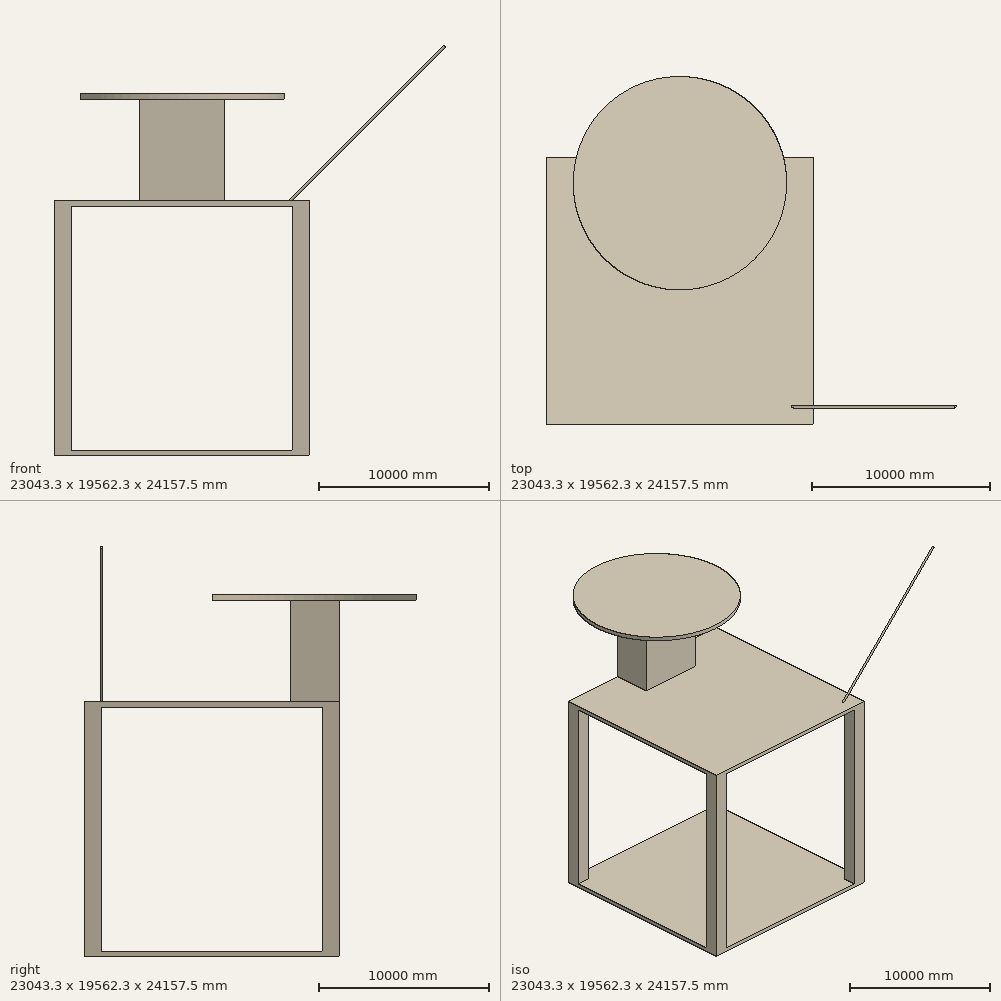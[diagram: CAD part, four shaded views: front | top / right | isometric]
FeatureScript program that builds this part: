
annotation { "Feature Type Name" : "Feature", "Feature Type Description" : "" }
export const myFeature = defineFeature(function(context is Context, id is Id, definition is map)
    precondition{}
    {
        {
            var Q0;
            Q0=qCreatedBy(makeId("Top.planeOp"),FACE);
            var sketch = newSketch(context, id + "F0", { "sketchPlane" : qUnion([Q0])});
            skLineSegment(sketch, "E0.bottom", {"start": v(-7500, 7500) * mm, "end": v(7500, 7500) * mm});
            skLineSegment(sketch, "E0.top", {"start": v(-7500, -7500) * mm, "end": v(7500, -7500) * mm});
            skLineSegment(sketch, "E0.left", {"start": v(-7500, 7500) * mm, "end": v(-7500, -7500) * mm});
            skLineSegment(sketch, "E0.right", {"start": v(7500, 7500) * mm, "end": v(7500, -7500) * mm});
            skSolve(sketch);
        }
        {
            var Q0;
            Q0=makeQuery(id+"F0.imprint","IMPRINT",FACE,{"disambiguationData":[TD([[makeQuery(id+"F0.imprint","IMPRINT",EDGE,{"derivedFrom":sQuery(id+"F0.wireOp",EDGE,"E0.bottom")}),-1.0]])]});
            extrude(context, id + "F1", {"entities" : qUnion([Q0]), "depth" : 15000 * mm, "offsetDistance" : 25 * mm});
        }
        {
            var Q0;
            Q0=makeQuery(id+"F1.opExtrude","SWEPT_FACE",FACE,{"disambiguationData":[OSD([sQuery(id+"F0.wireOp",EDGE,"E0.top")])]});
            var sketch = newSketch(context, id + "F2", { "sketchPlane" : qUnion([Q0])});
            skLineSegment(sketch, "E1", {"start": v(-6500, 300) * mm, "end": v(6500, 300) * mm});
            skLineSegment(sketch, "E2", {"start": v(-6500, 300) * mm, "end": v(-6500, 14700) * mm});
            skLineSegment(sketch, "E3", {"start": v(-6500, 14700) * mm, "end": v(6500, 14700) * mm});
            skLineSegment(sketch, "E4", {"start": v(6500, 14700) * mm, "end": v(6500, 300) * mm});
            skSolve(sketch);
        }
        {
            var Q0;
            Q0=makeQuery(id+"F2.imprint","IMPRINT",FACE,{"disambiguationData":[TD([[makeQuery(id+"F2.imprint","IMPRINT",EDGE,{"derivedFrom":sQuery(id+"F2.wireOp",EDGE,"E1")}),1.0]])]});
            extrude(context, id + "F3", {"entities" : qUnion([Q0]), "operationType" : NewBodyOperationType.REMOVE, "endBound" : BoundingType.THROUGH_ALL, "oppositeDirection" : true, "depth" : 25 * mm, "offsetDistance" : 25 * mm});
        }
        {
            var Q0;
            Q0=makeQuery(id+"F1.opExtrude","SWEPT_FACE",FACE,{"disambiguationData":[OSD([sQuery(id+"F0.wireOp",EDGE,"E0.left")])]});
            var sketch = newSketch(context, id + "F4", { "sketchPlane" : qUnion([Q0])});
            skLineSegment(sketch, "E5.bottom", {"start": v(-6500, 14700) * mm, "end": v(6500, 14700) * mm});
            skLineSegment(sketch, "E5.top", {"start": v(-6500, 300) * mm, "end": v(6500, 300) * mm});
            skLineSegment(sketch, "E5.left", {"start": v(-6500, 14700) * mm, "end": v(-6500, 300) * mm});
            skLineSegment(sketch, "E5.right", {"start": v(6500, 14700) * mm, "end": v(6500, 300) * mm});
            skSolve(sketch);
        }
        {
            var Q0;
            Q0=makeQuery(id+"F4.imprint","IMPRINT",FACE,{"disambiguationData":[TD([[makeQuery(id+"F4.imprint","IMPRINT",EDGE,{"derivedFrom":sQuery(id+"F4.wireOp",EDGE,"E5.bottom")}),-1.0]])]});
            extrude(context, id + "F5", {"entities" : qUnion([Q0]), "operationType" : NewBodyOperationType.REMOVE, "endBound" : BoundingType.THROUGH_ALL, "oppositeDirection" : true, "depth" : 25 * mm, "offsetDistance" : 25 * mm});
        }
        {
            var Q0;
            Q0=makeQuery(id+"F1.opExtrude","CAP_FACE",FACE,{"disambiguationData":[OSD([sQuery(id+"F0.wireOp",EDGE,"E0.bottom"),sQuery(id+"F0.wireOp",EDGE,"E0.top"),sQuery(id+"F0.wireOp",EDGE,"E0.left"),sQuery(id+"F0.wireOp",EDGE,"E0.right")])],"isStart":false});
            var sketch = newSketch(context, id + "F6", { "sketchPlane" : qUnion([Q0])});
            skLineSegment(sketch, "E6.bottom", {"start": v(-2500, 7500) * mm, "end": v(2500, 7500) * mm});
            skLineSegment(sketch, "E6.top", {"start": v(-2500, 4624.62) * mm, "end": v(2500, 4624.62) * mm});
            skLineSegment(sketch, "E6.left", {"start": v(-2500, 7500) * mm, "end": v(-2500, 4624.62) * mm});
            skLineSegment(sketch, "E6.right", {"start": v(2500, 7500) * mm, "end": v(2500, 4624.62) * mm});
            skSolve(sketch);
        }
        {
            var Q0;
            Q0=makeQuery(id+"F6.imprint","IMPRINT",FACE,{"disambiguationData":[TD([[makeQuery(id+"F6.imprint","IMPRINT",EDGE,{"derivedFrom":sQuery(id+"F6.wireOp",EDGE,"E6.bottom")}),-1.0]])]});
            extrude(context, id + "F7", {"entities" : qUnion([Q0]), "operationType" : NewBodyOperationType.ADD, "depth" : 6000 * mm, "offsetDistance" : 25 * mm});
        }
        {
            var Q0;
            Q0=makeQuery(id+"F7.opExtrude","CAP_FACE",FACE,{"disambiguationData":[OSD([sQuery(id+"F6.wireOp",EDGE,"E6.bottom"),sQuery(id+"F6.wireOp",EDGE,"E6.top"),sQuery(id+"F6.wireOp",EDGE,"E6.left"),sQuery(id+"F6.wireOp",EDGE,"E6.right")])],"isStart":false});
            var sketch = newSketch(context, id + "F8", { "sketchPlane" : qUnion([Q0])});
            skLineSegment(sketch, "E7", {"start": v(-2500, 6062.3) * mm, "end": v(2500, 6062.3) * mm, "construction": true});
            skLineSegment(sketch, "E8", {"start": v(0, 4624.62) * mm, "end": v(0, 7500) * mm, "construction": true});
            skCircle(sketch, "E9", {"center": v(0, 6062.3) * mm, "radius": 6000 * mm});
            skSolve(sketch);
        }
        {
            var Q0;
            Q0=makeQuery(id+"F8.imprint","IMPRINT",FACE,{"disambiguationData":[TD([[makeQuery(id+"F8.imprint","IMPRINT",EDGE,{"derivedFrom":sQuery(id+"F8.wireOp",EDGE,"E9")}),1.0]])]});
            var Q1;
            Q1=makeQuery(id+"F8.imprint","IMPRINT",FACE,{"disambiguationData":[TD([[makeQuery(id+"F8.imprint","IMPRINT",EDGE,{"derivedFrom":makeQuery(id+"F7.opExtrude","CAP_EDGE",EDGE,{"disambiguationData":[OSD([sQuery(id+"F6.wireOp",EDGE,"E6.bottom")])],"isStart":false})}),-1.0]])]});
            extrude(context, id + "F9", {"entities" : qUnion([Q0, Q1]), "operationType" : NewBodyOperationType.ADD, "depth" : 300 * mm, "offsetDistance" : 25 * mm});
        }
        {
            var Q0;
            Q0=makeQuery(id+"F1.opExtrude","CAP_FACE",FACE,{"disambiguationData":[OSD([sQuery(id+"F0.wireOp",EDGE,"E0.bottom"),sQuery(id+"F0.wireOp",EDGE,"E0.top"),sQuery(id+"F0.wireOp",EDGE,"E0.left"),sQuery(id+"F0.wireOp",EDGE,"E0.right")])],"isStart":false});
            var sketch = newSketch(context, id + "F10", { "sketchPlane" : qUnion([Q0])});
            skCircle(sketch, "E10", {"center": v(6500, -6500) * mm, "radius": 75 * mm});
            skSolve(sketch);
        }
        {
            var Q0;
            Q0=makeQuery(id+"F10.imprint","IMPRINT",FACE,{"disambiguationData":[TD([[makeQuery(id+"F10.imprint","IMPRINT",EDGE,{"derivedFrom":sQuery(id+"F10.wireOp",EDGE,"E10")}),1.0]])]});
            extrude(context, id + "F11", {"entities" : qUnion([Q0]), "depth" : 12000 * mm, "offsetDistance" : 25 * mm});
        }
        {
            var Q0;
            Q0=makeQuery(id+"F11.opExtrude","SWEPT_BODY",BODY,{"disambiguationData":[OSD([sQuery(id+"F10.wireOp",EDGE,"E10")])]});
            var Q1;
            Q1=makeQuery(id+"F5.boolean.opBoolean","INTERSECT",EDGE,{"derivedFrom":[makeQuery(id+"F1.opExtrude","SWEPT_FACE",FACE,{"disambiguationData":[OSD([sQuery(id+"F0.wireOp",EDGE,"E0.right")])]}),makeQuery(id+"F5.opExtrude","SWEPT_FACE",FACE,{"disambiguationData":[OSD([sQuery(id+"F4.wireOp",EDGE,"E5.bottom")])]})]});
            transform(context, id + "F12", {"entities" : qUnion([Q0]), "transformType" : TransformType.ROTATION, "transformAxis" : qUnion([Q1]), "angle" : 45 * degree, "makeCopy" : false});
        }
        {
            var Q0;
            Q0=makeQuery(id+"F11.opExtrude","CAP_FACE",FACE,{"disambiguationData":[OSD([sQuery(id+"F10.wireOp",EDGE,"E10")])],"isStart":true});
            var sketch = newSketch(context, id + "F13", { "sketchPlane" : qUnion([Q0])});
            skCircle(sketch, "E11", {"center": v(6500, 6091.17) * mm, "radius": 75 * mm});
            skSolve(sketch);
        }
        {
            var Q0;
            Q0=makeQuery(id+"F13.imprint","IMPRINT",FACE,{"disambiguationData":[TD([[makeQuery(id+"F13.imprint","IMPRINT",EDGE,{"derivedFrom":sQuery(id+"F13.wireOp",EDGE,"E11")}),-1.0]])]});
            var Q1;
            Q1=makeQuery(id+"F1.opExtrude","CAP_FACE",FACE,{"disambiguationData":[OSD([sQuery(id+"F0.wireOp",EDGE,"E0.bottom"),sQuery(id+"F0.wireOp",EDGE,"E0.top"),sQuery(id+"F0.wireOp",EDGE,"E0.left"),sQuery(id+"F0.wireOp",EDGE,"E0.right")])],"isStart":false});
            extrude(context, id + "F14", {"entities" : qUnion([Q0]), "operationType" : NewBodyOperationType.ADD, "endBound" : BoundingType.UP_TO_SURFACE, "depth" : 25 * mm, "endBoundEntityFace" : qUnion([Q1]), "offsetDistance" : 25 * mm});
        }
    });
